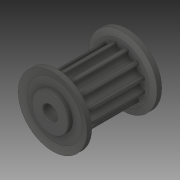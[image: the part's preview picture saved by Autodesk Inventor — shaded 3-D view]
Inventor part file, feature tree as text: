
AUTODESK INVENTOR PART (.ipt)
format: ipt  version: 2019 (Build 230136000, 136)  size: 213,504 bytes
history: native  units: in
note: dims shown in document units (in); Inventor stores cm internally (conversion verified against a paired STEP export)
features: chamfer x1
ambient origin geometry x8: Origin, YZ Plane, XZ Plane, XY Plane, X Axis, Y Axis, Z Axis, Center Point
bodies: Solid1 (feature_tree)
feature tree (1):
  chamfer  "Chamfer1"  [1 undecoded]
note: 1 required parameter value undecoded (feature->parameter linkage not recoverable at this tier; creation-order binding heuristic only, values carry confidence <= 0.55)
